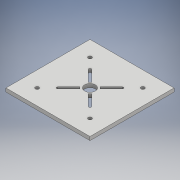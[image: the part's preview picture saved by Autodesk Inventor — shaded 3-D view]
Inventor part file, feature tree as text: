
AUTODESK INVENTOR PART (.ipt)
format: ipt  version: 2017 (Build 210142000, 142)  size: 134,144 bytes
history: native  units: mm
features: extrude x1, sketch x1
ambient origin geometry x8: Origin, YZ Plane, XZ Plane, XY Plane, X Axis, Y Axis, Z Axis, Center Point
bodies: Body1 (feature_tree)
feature tree (2):
  extrude  "Extrusion4"  Depth=3.0mm
  sketch  "Sketch1"  dims[d12=3.0mm d13=3.0mm d14=3.0mm d15=3.0mm d55=70.0mm d56=70.0mm d57=3.0mm d58=0.0mm]
